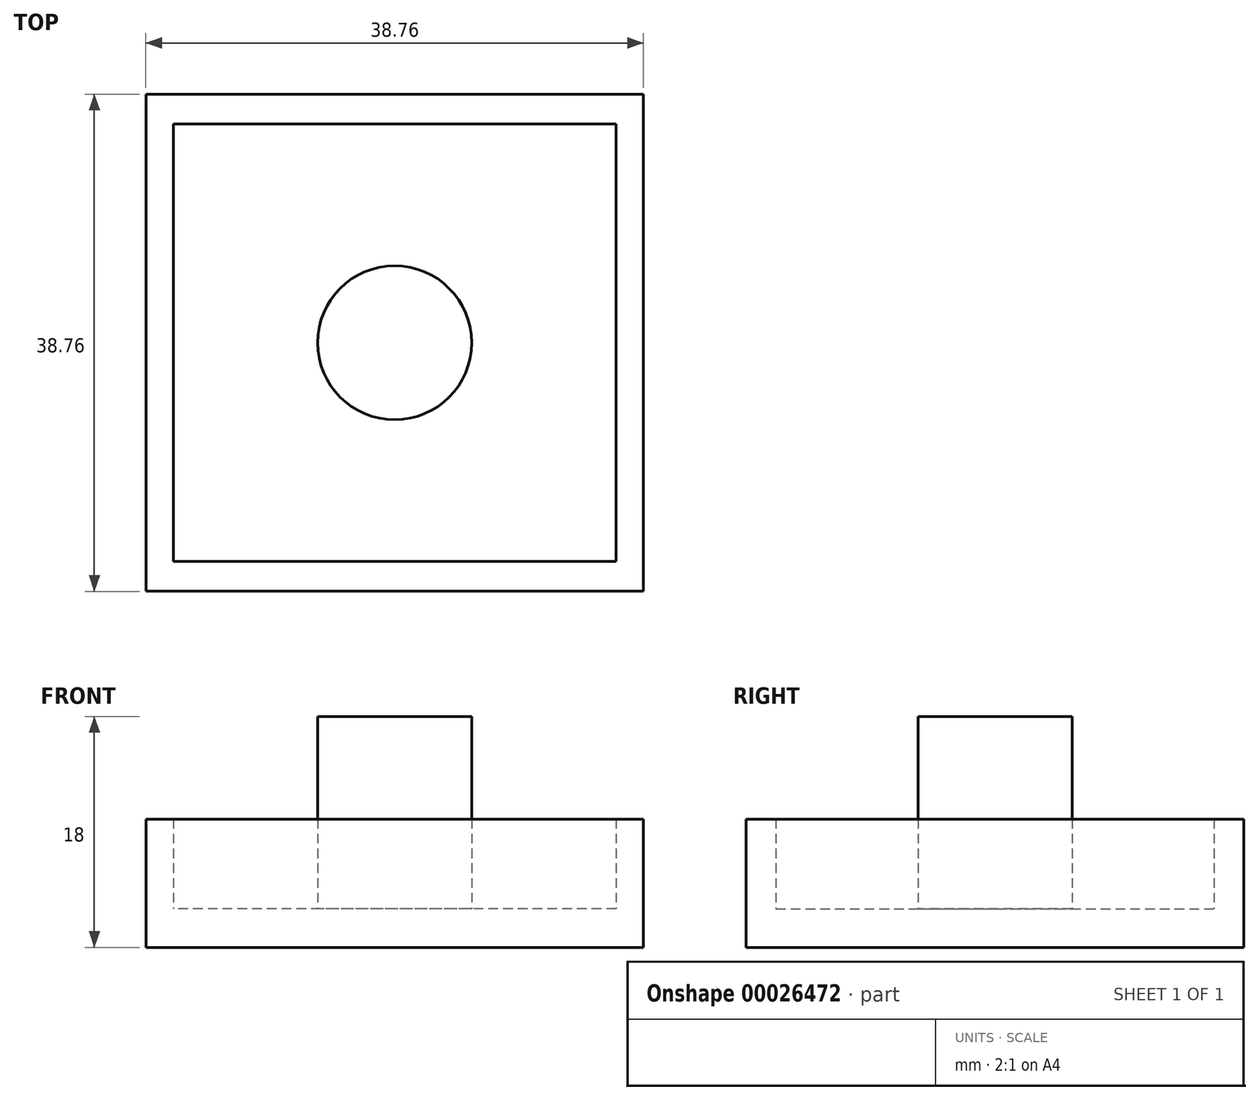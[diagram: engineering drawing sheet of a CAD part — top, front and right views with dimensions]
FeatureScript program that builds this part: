
annotation { "Feature Type Name" : "Feature", "Feature Type Description" : "" }
export const myFeature = defineFeature(function(context is Context, id is Id, definition is map)
    precondition{}
    {
        {
            var Q0;
            Q0=qCreatedBy(makeId("Top.planeOp"),FACE);
            var sketch = newSketch(context, id + "F0", { "sketchPlane" : qUnion([Q0])});
            skLineSegment(sketch, "E0.rect.bottom", {"start": v(19.38, 19.38) * mm, "end": v(-19.38, 19.38) * mm});
            skLineSegment(sketch, "E0.rect.top", {"start": v(19.38, -19.37) * mm, "end": v(-19.38, -19.37) * mm});
            skLineSegment(sketch, "E0.rect.left", {"start": v(19.38, 19.38) * mm, "end": v(19.38, -19.37) * mm});
            skLineSegment(sketch, "E0.rect.right", {"start": v(-19.38, 19.38) * mm, "end": v(-19.38, -19.37) * mm});
            skPoint(sketch, "E0.rect.middle", {"position": v(0, 0) * mm});
            skSolve(sketch);
        }
        {
            var Q0;
            Q0 = qSketchRegion(id + "F0", true);
            extrude(context, id + "F1", {"entities" : qUnion([Q0]), "depth" : 3 * mm});
        }
        {
            var Q0;
            Q0=makeQuery(id+"F1.opExtrude","CAP_FACE",FACE,{"disambiguationData":[OSD([sQuery(id+"F0.wireOp",EDGE,"E0.rect.bottom"),sQuery(id+"F0.wireOp",EDGE,"E0.rect.top"),sQuery(id+"F0.wireOp",EDGE,"E0.rect.left"),sQuery(id+"F0.wireOp",EDGE,"E0.rect.right")])],"isStart":false});
            var sketch = newSketch(context, id + "F2", { "sketchPlane" : qUnion([Q0])});
            skLineSegment(sketch, "E1.rect.bottom", {"start": v(19.38, -19.37) * mm, "end": v(-19.38, -19.37) * mm});
            skLineSegment(sketch, "E1.rect.top", {"start": v(19.38, 19.37) * mm, "end": v(-19.38, 19.37) * mm});
            skLineSegment(sketch, "E1.rect.left", {"start": v(19.38, -19.37) * mm, "end": v(19.38, 19.37) * mm});
            skLineSegment(sketch, "E1.rect.right", {"start": v(-19.38, -19.37) * mm, "end": v(-19.38, 19.37) * mm});
            skPoint(sketch, "E1.rect.middle", {"position": v(0, 0) * mm});
            skLineSegment(sketch, "E2.rect.bottom", {"start": v(17.25, -17.05) * mm, "end": v(-17.25, -17.05) * mm});
            skLineSegment(sketch, "E2.rect.top", {"start": v(17.25, 17.05) * mm, "end": v(-17.25, 17.05) * mm});
            skLineSegment(sketch, "E2.rect.left", {"start": v(17.25, -17.05) * mm, "end": v(17.25, 17.05) * mm});
            skLineSegment(sketch, "E2.rect.right", {"start": v(-17.25, -17.05) * mm, "end": v(-17.25, 17.05) * mm});
            skLineSegment(sketch, "E3", {"start": v(0, 0) * mm, "end": v(17.25, 0) * mm, "construction": true});
            skSolve(sketch);
        }
        {
            var Q0;
            Q0 = qSketchRegion(id + "F2", true);
            extrude(context, id + "F3", {"entities" : qUnion([Q0]), "operationType" : NewBodyOperationType.ADD, "depth" : 7 * mm});
        }
        {
            var Q0;
            Q0=makeQuery(id+"F1.opExtrude","CAP_FACE",FACE,{"disambiguationData":[OSD([sQuery(id+"F0.wireOp",EDGE,"E0.rect.bottom"),sQuery(id+"F0.wireOp",EDGE,"E0.rect.top"),sQuery(id+"F0.wireOp",EDGE,"E0.rect.left"),sQuery(id+"F0.wireOp",EDGE,"E0.rect.right")])],"isStart":false});
            var sketch = newSketch(context, id + "F4", { "sketchPlane" : qUnion([Q0])});
            skCircle(sketch, "E4", {"center": v(0, 0) * mm, "radius": 6 * mm});
            skSolve(sketch);
        }
        {
            var Q0;
            Q0 = qSketchRegion(id + "F4", true);
            extrude(context, id + "F5", {"entities" : qUnion([Q0]), "operationType" : NewBodyOperationType.ADD, "depth" : 15 * mm});
        }
    });
